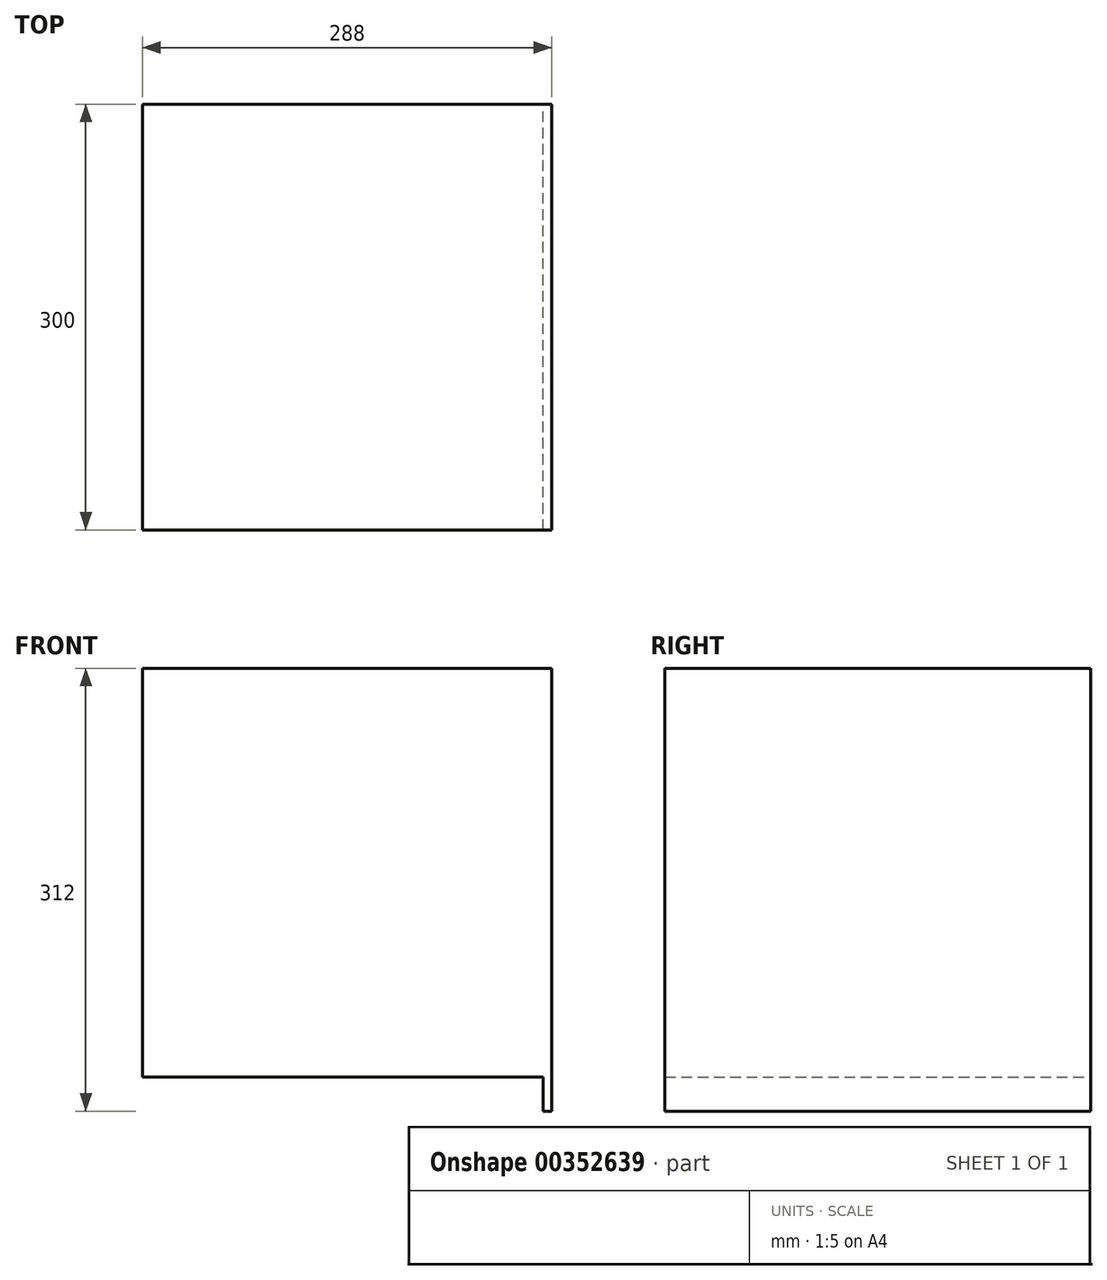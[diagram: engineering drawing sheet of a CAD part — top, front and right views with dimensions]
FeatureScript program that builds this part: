
annotation { "Feature Type Name" : "Feature", "Feature Type Description" : "" }
export const myFeature = defineFeature(function(context is Context, id is Id, definition is map)
    precondition{}
    {
        {
            var Q0;
            Q0=qCreatedBy(makeId("Front.planeOp"),FACE);
            var sketch = newSketch(context, id + "F0", { "sketchPlane" : qUnion([Q0])});
            skLineSegment(sketch, "E0.bottom", {"start": v(-240.7, 251.43) * mm, "end": v(47.3, 251.43) * mm});
            skLineSegment(sketch, "E0.top", {"start": v(41.3, -60.57) * mm, "end": v(47.3, -60.57) * mm});
            skLineSegment(sketch, "E0.left", {"start": v(-240.7, 251.43) * mm, "end": v(-240.7, -36.57) * mm});
            skLineSegment(sketch, "E0.right", {"start": v(47.3, 251.43) * mm, "end": v(47.3, -60.57) * mm});
            skLineSegment(sketch, "E1", {"start": v(41.3, -60.57) * mm, "end": v(41.3, -36.57) * mm});
            skLineSegment(sketch, "E2", {"start": v(41.3, -36.57) * mm, "end": v(-240.7, -36.57) * mm});
            skSolve(sketch);
        }
        {
            var Q0;
            Q0=qSketchRegion(id+"F0",true);
            extrude(context, id + "F1", {"entities" : qUnion([Q0]), "depth" : 300 * mm});
        }
    });
